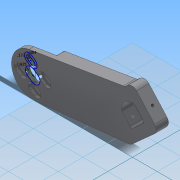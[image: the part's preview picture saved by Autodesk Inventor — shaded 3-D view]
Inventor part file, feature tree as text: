
AUTODESK INVENTOR PART (.ipt)
format: ipt  version: 2014 SP2 (Build 180246200, 246)  size: 322,048 bytes
history: native  units: in
note: dims shown in document units (in); Inventor stores cm internally (conversion verified against a paired STEP export)
features: other x15, extrude x5, fillet x4, sketch x3, hole x2, pattern_linear x1
ambient origin geometry x8: Origin, YZ Plane, XZ Plane, XY Plane, X Axis, Y Axis, Z Axis, Center Point
bodies: Solid4 (feature_tree)
feature tree (30):
  other  "Blocks"
  other  "Base Sketch"
  extrude  "Base"  Depth=0.4in
  other  "Motor Hole Sketch"
  extrude  "Motor Hole"  Depth=0.4in
  extrude  "Motor Cbore"  Depth=0.5in TaperAngle=0.0deg
  pattern_linear  "Rectangular Pattern1"  Spacing1=-0.5in  [1 undecoded]
  extrude  "Motor Axle"  Depth=0.3125in
  other  "Back Plane"
  extrude  "Pocket"  TaperAngle=0.0deg  [1 undecoded]
  other  "Midplane"
  sketch  "Sketch15"  dims[d98=0.4in d99=0.4in]
  sketch  "Sketch16"  dims[d116=0.0in d130=0.5in d131=0.0in d134=-0.5in d135=0.3125in d136=0.0in d153=0.25in d155=0.125in d157=1.7in d158=0.25in d168=0.337in d167=-0.25in d176=0.3in d177=0.3in d178=0.3in d179=0.6323in d180=0.6323in d182=0.125in d183=0.25in d186=0.6066in d187=0.6066in d188=0.09in d189=0.9843in d192=0.4882in d193=0.1772in d195=0.3543in d197=0.9843in d209=4.1506in d211=0.4252in d212=0.7874in d214=0.6955in d215=0.7874in d217=0.6955in d218=0.3543in d219=0.1181in d220=0.0in d221=0.1181in d222=0.0in d226=0.25in d228=1.9291in d229=0.1in d231=0.78in d233=1.9291in d235=0.25in d236=0.25in d237=0.104in d238=0.75in d239=0.375in d240=0.25in d241=0.5635in d242=1.0in d243=0.8108in d244=0.104in d245=0.75in d246=0.375in d247=0.25in d248=0.5635in d249=1.0in d250=0.8108in d251=0.25in d252=0.1in d169=1.0in]
  hole  "Hole3"  [1 undecoded]
  hole  "Hole4"  [1 undecoded]
  fillet  "Fillet1"  Radius=1.7in
  fillet  "Fillet2"  Radius=0.25in
  fillet  "Fillet3"  [1 undecoded]
  fillet  "Fillet4"  Radius=0.3in
  other  "the Axle"
  other  "Motor Mount Pattern"
  sketch  "Sketch12"  dims[d84=0.715in d85=0.9482in d97=0.4in]
  other  "Motor Body Extent"
  other  "Block7"
  other  "MotorMountPattern"
  other  "AxleOutline"
  other  "Motor Mount Pattern:4"
  other  "Motor Mount Pattern:5"
  other  "Motor Mount Pattern:6"
  other  "MotorMountPattern:1"
note: 5 required parameter values undecoded (feature->parameter linkage not recoverable at this tier; creation-order binding heuristic only, values carry confidence <= 0.55)
